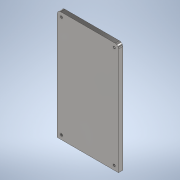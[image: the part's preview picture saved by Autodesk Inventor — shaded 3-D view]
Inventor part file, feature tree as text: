
AUTODESK INVENTOR PART (.ipt)
format: ipt  version: 2021 (Build 250183000, 183)  size: 122,368 bytes
history: native  units: mm
features: fillet x2, sketch x2, extrude x1, hole x1, projected_geometry x1
ambient origin geometry x8: Origin, YZ Plane, XZ Plane, XY Plane, X Axis, Y Axis, Z Axis, Center Point
bodies: Solid1 (feature_tree)
feature tree (7):
  extrude  "Extrusion1"  Depth=130.0mm
  fillet  "Fillet1"  Radius=5.0mm
  fillet  "Fillet2"  Radius=4.0mm
  hole  "Hole1"  [1 undecoded]
  sketch  "Sketch1"  dims[d0=72.0mm d1=130.0mm d2=5.0mm d3=0.0mm d4=4.0mm]
  sketch  "Sketch2"  dims[d5=4.0mm d7=3.0mm d8=5.0mm d9=5.0mm d10=3.0mm d11=5.0mm d12=5.0mm d13=2.6416mm d14=7.01mm d15=4.0mm d16=2.0mm d17=90.0deg d18=10.979mm d19=0.0mm]
  projected_geometry  "Projected Loop1"
note: 1 required parameter value undecoded (feature->parameter linkage not recoverable at this tier; creation-order binding heuristic only, values carry confidence <= 0.55)
